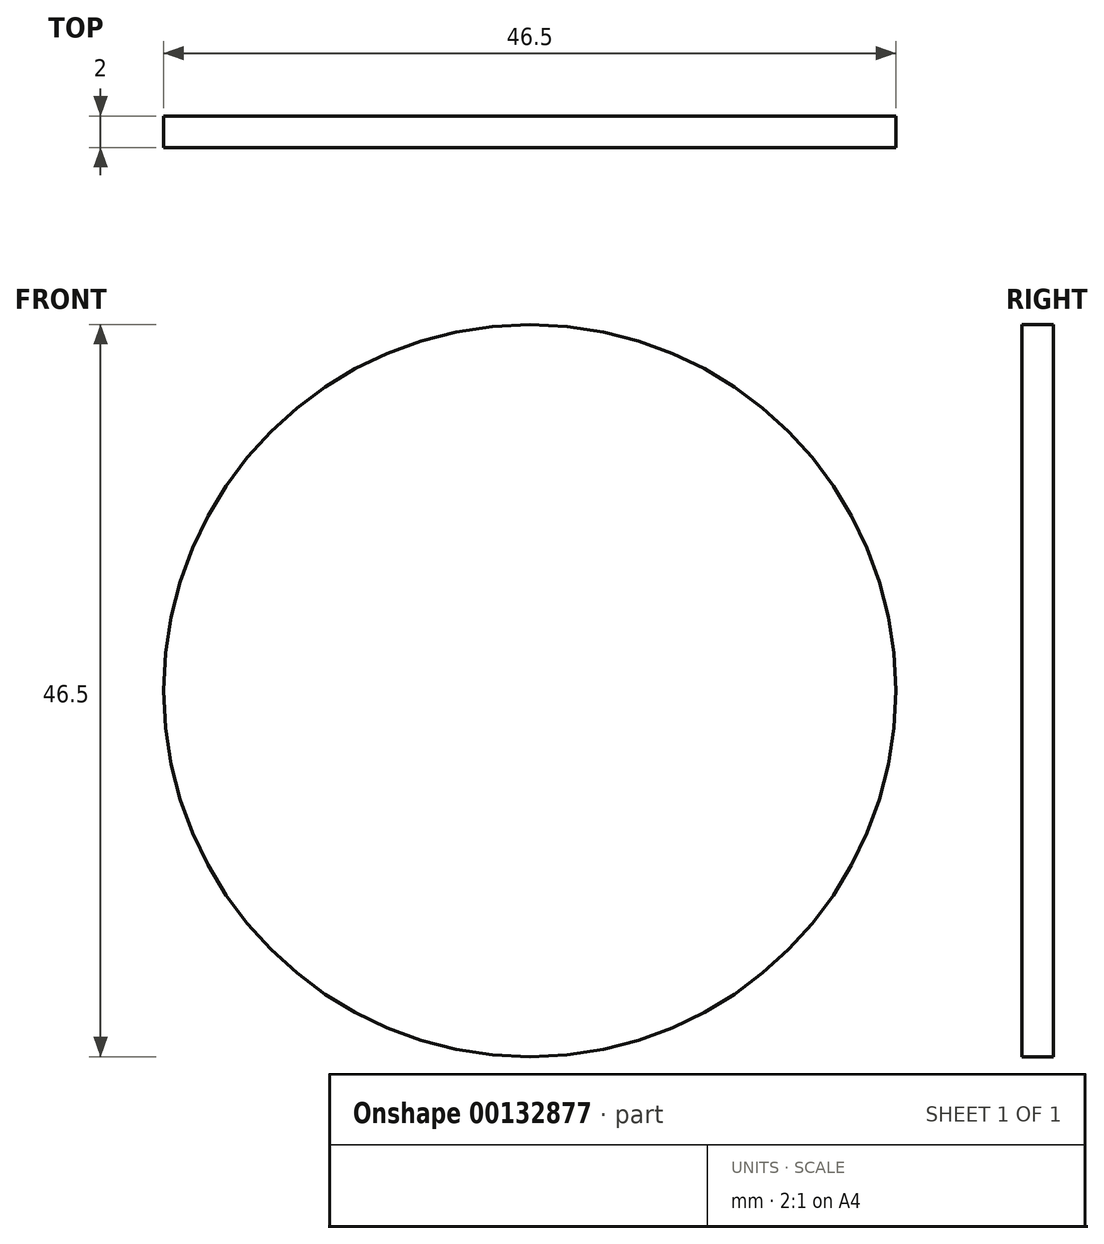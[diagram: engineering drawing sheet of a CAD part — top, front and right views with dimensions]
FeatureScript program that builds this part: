
annotation { "Feature Type Name" : "Feature", "Feature Type Description" : "" }
export const myFeature = defineFeature(function(context is Context, id is Id, definition is map)
    precondition{}
    {
        {
            var Q0;
            Q0=qCreatedBy(makeId("Front.planeOp"),FACE);
            var sketch = newSketch(context, id + "F0", { "sketchPlane" : qUnion([Q0])});
            skCircle(sketch, "E0", {"center": v(0, 0) * mm, "radius": 23.25 * mm});
            skSolve(sketch);
        }
        {
            var Q0;
            Q0 = qSketchRegion(id + "F0", true);
            extrude(context, id + "F1", {"entities" : qUnion([Q0]), "depth" : 2 * mm});
        }
    });
